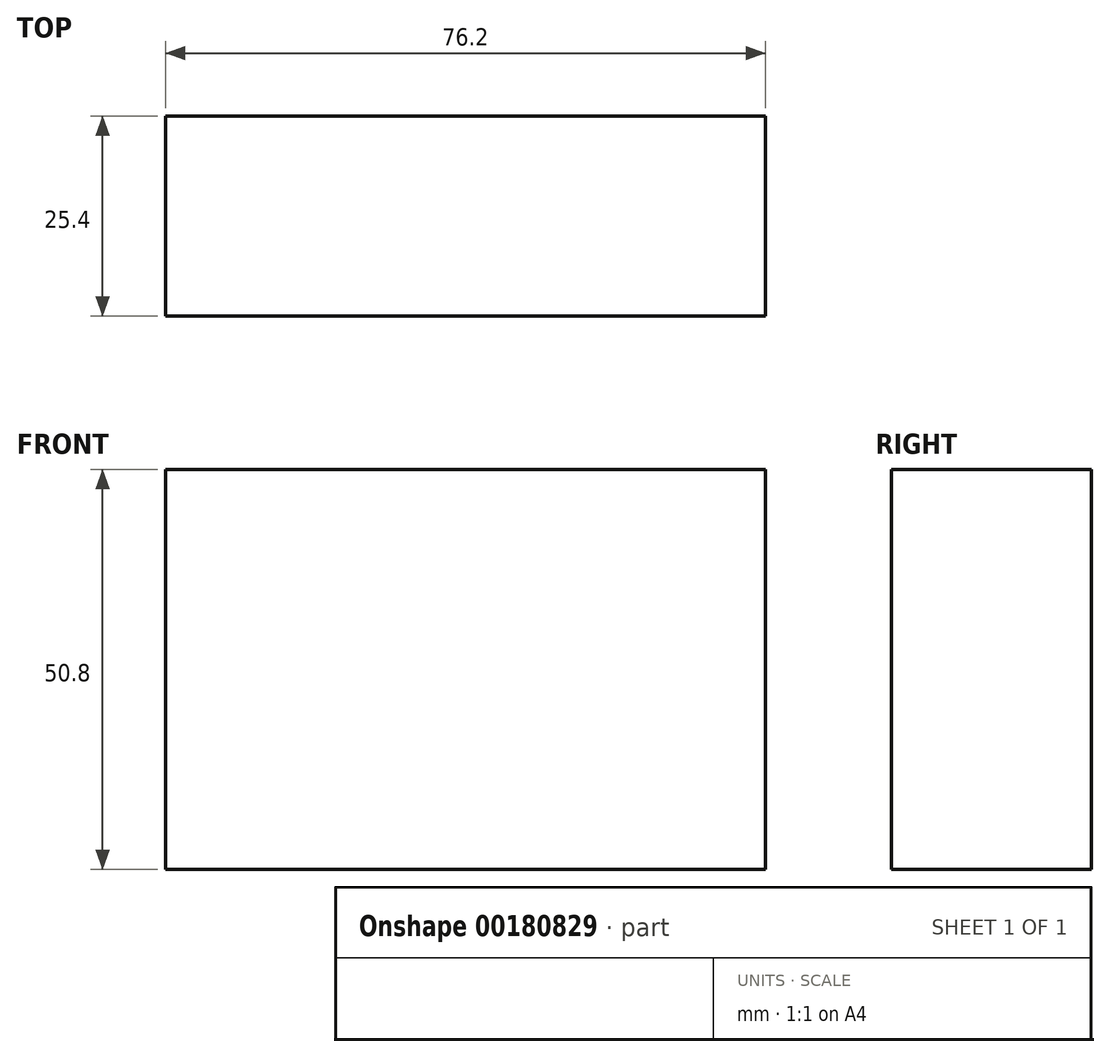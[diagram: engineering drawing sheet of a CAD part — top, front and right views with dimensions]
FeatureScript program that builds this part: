
annotation { "Feature Type Name" : "Feature", "Feature Type Description" : "" }
export const myFeature = defineFeature(function(context is Context, id is Id, definition is map)
    precondition{}
    {
        {
            var Q0;
            Q0=qCreatedBy(makeId("Front.planeOp"),FACE);
            var sketch = newSketch(context, id + "F0", { "sketchPlane" : qUnion([Q0])});
            skCircle(sketch, "E0", {"center": v(0, 0) * mm, "radius": 25.4 * mm});
            skLineSegment(sketch, "E1.bottom", {"start": v(38.1, -25.4) * mm, "end": v(-38.1, -25.4) * mm});
            skLineSegment(sketch, "E1.top", {"start": v(38.1, 25.4) * mm, "end": v(-38.1, 25.4) * mm});
            skLineSegment(sketch, "E1.left", {"start": v(38.1, -25.4) * mm, "end": v(38.1, 25.4) * mm});
            skLineSegment(sketch, "E1.right", {"start": v(-38.1, -25.4) * mm, "end": v(-38.1, 25.4) * mm});
            skSolve(sketch);
        }
        {
            var Q0;
            Q0=sQuery(id+"F0.wireOp",EDGE,"E0");
            extrude(context, id + "F1", {"bodyType" : ToolBodyType.SURFACE, "surfaceEntities" : qUnion([Q0]), "depth" : 101.6 * mm});
        }
        {
            var Q0;
            Q0 = qSketchRegion(id + "F0", true);
            extrude(context, id + "F2", {"entities" : qUnion([Q0]), "depth" : 25.4 * mm});
        }
    });
